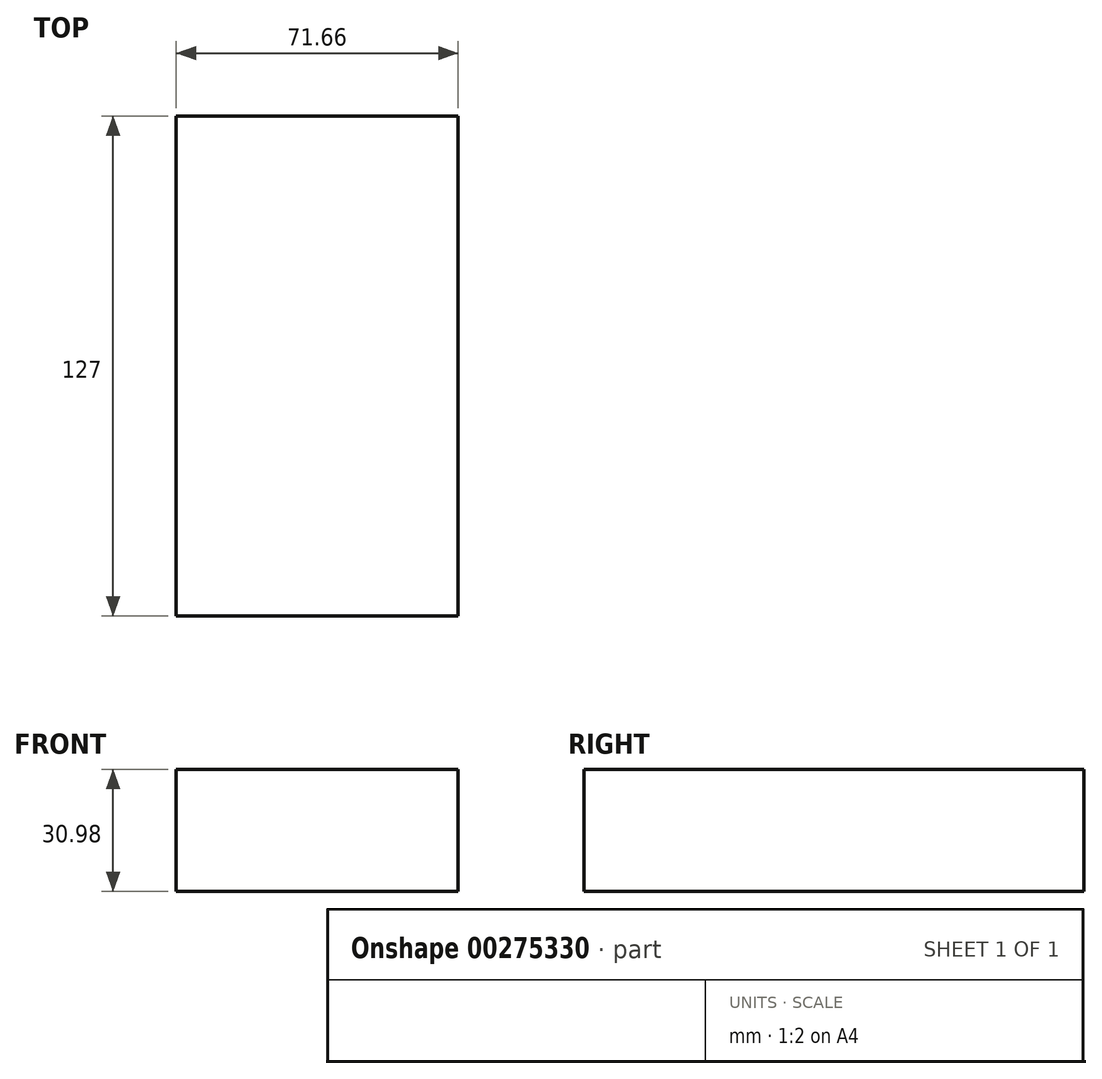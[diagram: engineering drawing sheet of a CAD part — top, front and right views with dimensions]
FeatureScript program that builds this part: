
annotation { "Feature Type Name" : "Feature", "Feature Type Description" : "" }
export const myFeature = defineFeature(function(context is Context, id is Id, definition is map)
    precondition{}
    {
        {
            var Q0;
            Q0=qCreatedBy(makeId("Front.planeOp"),FACE);
            var sketch = newSketch(context, id + "F0", { "sketchPlane" : qUnion([Q0])});
            skLineSegment(sketch, "E0.bottom", {"start": v(35.83, -15.49) * mm, "end": v(-35.83, -15.49) * mm});
            skLineSegment(sketch, "E0.top", {"start": v(35.83, 15.49) * mm, "end": v(-35.83, 15.49) * mm});
            skLineSegment(sketch, "E0.left", {"start": v(35.83, -15.49) * mm, "end": v(35.83, 15.49) * mm});
            skLineSegment(sketch, "E0.right", {"start": v(-35.83, -15.49) * mm, "end": v(-35.83, 15.49) * mm});
            skPoint(sketch, "E0.middle", {"position": v(0, 0) * mm});
            skLineSegment(sketch, "E1.bottom", {"start": v(71.85, 65.5) * mm, "end": v(136.41, 65.5) * mm});
            skLineSegment(sketch, "E1.top", {"start": v(71.85, 37.88) * mm, "end": v(136.41, 37.88) * mm});
            skLineSegment(sketch, "E1.left", {"start": v(71.85, 65.5) * mm, "end": v(71.85, 37.88) * mm});
            skLineSegment(sketch, "E1.right", {"start": v(136.41, 65.5) * mm, "end": v(136.41, 37.88) * mm});
            skPoint(sketch, "E1.middle", {"position": v(104.13, 51.7) * mm});
            skLineSegment(sketch, "E2", {"start": v(35.83, 15.49) * mm, "end": v(35.83, 32.66) * mm});
            skArc(sketch, "E3", {"start": v(35.83, 32.66) * mm, "mid": v(39.23, 41.72) * mm, "end": v(47.76, 46.3) * mm});
            skLineSegment(sketch, "E4", {"start": v(47.76, 46.3) * mm, "end": v(95, 46.3) * mm});
            skLineSegment(sketch, "E5.0", {"start": v(46.94, 61.3) * mm, "end": v(95, 61.3) * mm});
            skArc(sketch, "E5.1", {"start": v(20.83, 32.66) * mm, "mid": v(28.34, 52.04) * mm, "end": v(46.94, 61.3) * mm});
            skLineSegment(sketch, "E5.2", {"start": v(20.83, 15.49) * mm, "end": v(20.83, 32.66) * mm});
            skLineSegment(sketch, "E6", {"start": v(95, 61.3) * mm, "end": v(95, 46.3) * mm});
            skFitSpline(sketch, "E7", {"points": [v(-35.83, 15.49) * mm, v(46.94, 61.3) * mm], "startDerivative": vector(26.87, 97.97) * mm, "endDerivative": vector(102.18, -4.75) * mm});
            skSolve(sketch);
        }
        {
            var Q0;
            Q0=makeQuery(id+"F0.imprint","IMPRINT",FACE,{"disambiguationData":[TD([[makeQuery(id+"F0.imprint","IMPRINT",EDGE,{"derivedFrom":sQuery(id+"F0.wireOp",EDGE,"E0.bottom")}),-1.0]])]});
            extrude(context, id + "F1", {"entities" : qUnion([Q0]), "endBound" : BoundingType.SYMMETRIC, "depth" : 127 * mm});
        }
    });
